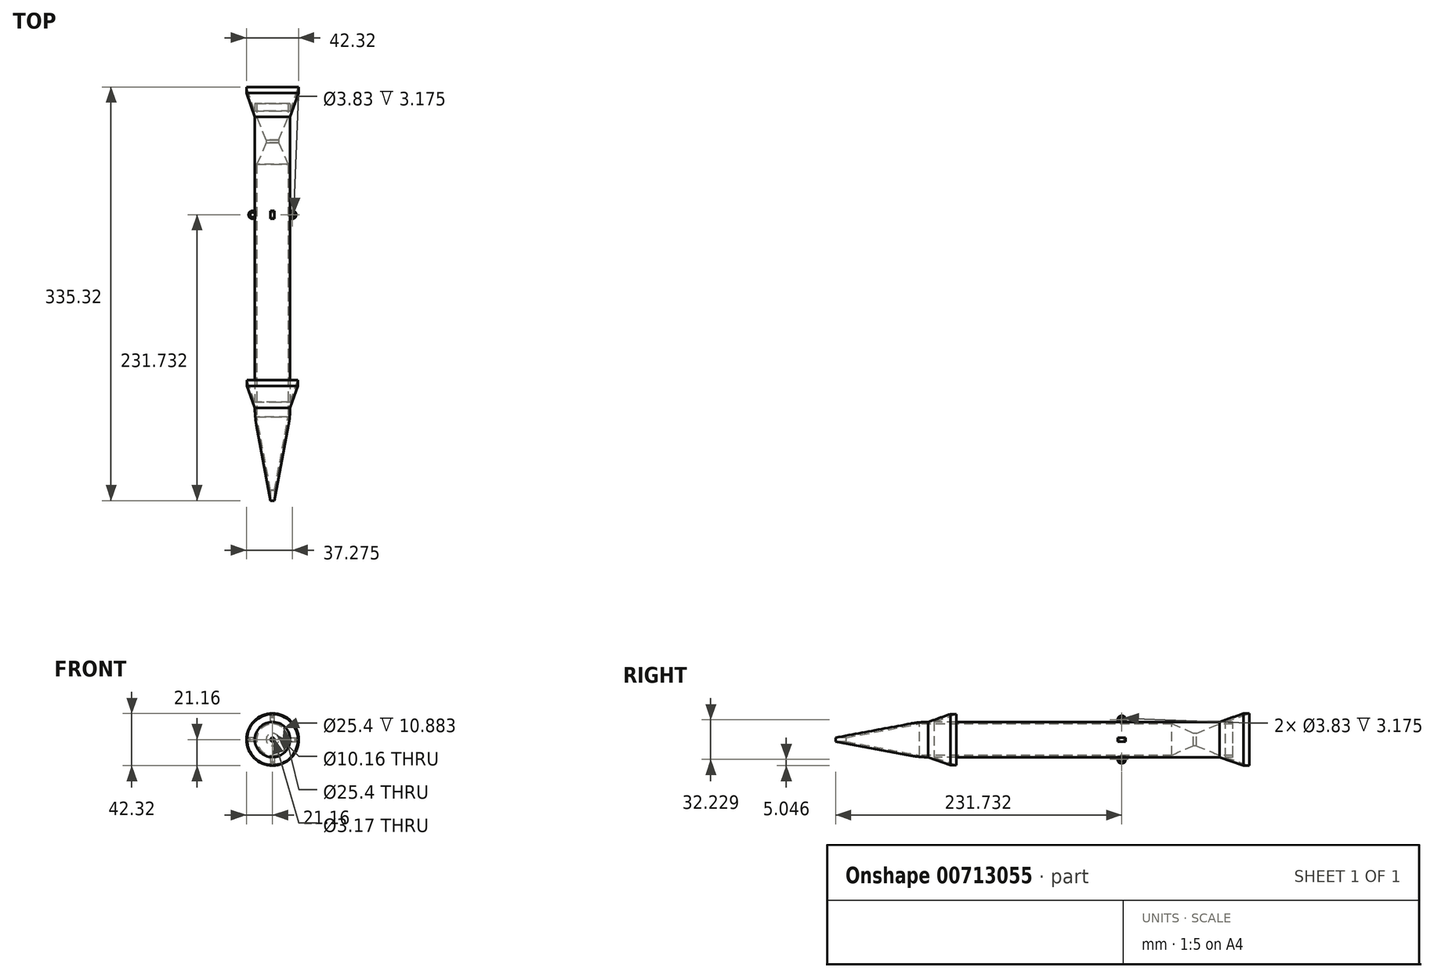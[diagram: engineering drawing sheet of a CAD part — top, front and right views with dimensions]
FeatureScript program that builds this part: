
annotation { "Feature Type Name" : "Feature", "Feature Type Description" : "" }
export const myFeature = defineFeature(function(context is Context, id is Id, definition is map)
    precondition{}
    {
        {
            var Q0;
            Q0=qCreatedBy(makeId("Front.planeOp"),FACE);
            var sketch = newSketch(context, id + "F0", { "sketchPlane" : qUnion([Q0])});
            skCircle(sketch, "E0", {"center": v(0, 0) * mm, "radius": 12.7 * mm});
            skCircle(sketch, "E1", {"center": v(0, 0) * mm, "radius": 14.29 * mm});
            skSolve(sketch);
        }
        {
            var Q0;
            Q0 = qSketchRegion(id + "F0", true);
            extrude(context, id + "F1", {"entities" : qUnion([Q0]), "oppositeDirection" : true, "depth" : 254 * mm, "offsetDistance" : 25.4 * mm});
        }
        {
            var Q0;
            Q0=qCreatedBy(makeId("Top.planeOp"),FACE);
            var sketch = newSketch(context, id + "F2", { "sketchPlane" : qUnion([Q0])});
            skLineSegment(sketch, "E2.0", {"start": v(14.29, 0) * mm, "end": v(-14.29, 0) * mm});
            skLineSegment(sketch, "E3", {"start": v(14.29, 0) * mm, "end": v(1.59, -68) * mm});
            skPoint(sketch, "E4", {"position": v(0, -68) * mm});
            skLineSegment(sketch, "E5", {"start": v(0, -68) * mm, "end": v(0, 0) * mm});
            skLineSegment(sketch, "E6", {"start": v(1.59, -68) * mm, "end": v(1.59, -59.5) * mm});
            skLineSegment(sketch, "E7", {"start": v(1.59, -59.5) * mm, "end": v(12.7, 0) * mm});
            skLineSegment(sketch, "E8.0", {"start": v(12.7, 0) * mm, "end": v(-12.7, 0) * mm});
            skPoint(sketch, "E9.orphan", {"position": v(-1.59, -68) * mm});
            skSolve(sketch);
        }
        {
            var Q0;
            Q0 = qSketchRegion(id + "F2", true);
            var Q1;
            Q1=sQuery(id+"F2.wireOp",EDGE,"E5");
            revolve(context, id + "F3", {"operationType" : NewBodyOperationType.ADD, "surfaceOperationType" : NewSurfaceOperationType.NEW, "entities" : qUnion([Q0]), "axis" : qUnion([Q1]), "revolveType" : RevolveType.FULL});
        }
        {
            var Q0;
            Q0=makeQuery(id+"F3.boolean.opBoolean","MERGE",EDGE,{"derivedFrom":[makeQuery(id+"F1.opExtrude","CAP_EDGE",EDGE,{"disambiguationData":[OSD([sQuery(id+"F0.wireOp",EDGE,"E1")])],"isStart":true}),makeQuery(id+"F3.opRevolve","SWEPT_EDGE",EDGE,{"disambiguationData":[OSD([sQuery(id+"F2.wireOp",EDGE,"E2.0"),sQuery(id+"F2.wireOp",EDGE,"E3")])]})]});
            fillet(context, id + "F4", {"entities" : qUnion([Q0]), "radius" : 76.2 * mm, "tangentPropagation" : true, "allowEdgeOverflow" : false});
        }
        {
            var Q0;
            Q0=qCreatedBy(makeId("Top.planeOp"),FACE);
            var sketch = newSketch(context, id + "F5", { "sketchPlane" : qUnion([Q0])});
            skLineSegment(sketch, "E10", {"start": v(14.29, 254) * mm, "end": v(14.29, 7.06) * mm});
            skLineSegment(sketch, "E11", {"start": v(14.29, 7.06) * mm, "end": v(20.64, 25.02) * mm});
            skLineSegment(sketch, "E12", {"start": v(20.64, 25.02) * mm, "end": v(20.64, 29.78) * mm});
            skLineSegment(sketch, "E13", {"start": v(20.64, 29.78) * mm, "end": v(14.29, 11.82) * mm});
            skLineSegment(sketch, "E14", {"start": v(14.29, 243.12) * mm, "end": v(21.16, 262.57) * mm});
            skLineSegment(sketch, "E15", {"start": v(21.16, 262.57) * mm, "end": v(21.16, 267.33) * mm});
            skLineSegment(sketch, "E16", {"start": v(21.16, 267.33) * mm, "end": v(14.29, 247.88) * mm});
            skLineSegment(sketch, "E17", {"start": v(0, 0) * mm, "end": v(0, 261.94) * mm});
            skSolve(sketch);
        }
        {
            var Q0;
            Q0 = qSketchRegion(id + "F5", true);
            var Q1;
            Q1=sQuery(id+"F5.wireOp",EDGE,"E17");
            revolve(context, id + "F6", {"operationType" : NewBodyOperationType.ADD, "surfaceOperationType" : NewSurfaceOperationType.NEW, "entities" : qUnion([Q0]), "axis" : qUnion([Q1]), "revolveType" : RevolveType.FULL});
        }
        {
            var Q0;
            Q0=qCreatedBy(makeId("Top.planeOp"),FACE);
            var sketch = newSketch(context, id + "F7", { "sketchPlane" : qUnion([Q0])});
            skLineSegment(sketch, "E18", {"start": v(14.29, 243.12) * mm, "end": v(14.29, 11.82) * mm});
            skLineSegment(sketch, "E19", {"start": v(14.29, 166.92) * mm, "end": v(16.2, 166.92) * mm});
            skLineSegment(sketch, "E20", {"start": v(14.29, 160.57) * mm, "end": v(16.2, 160.57) * mm});
            skArc(sketch, "E21", {"start": v(16.2, 160.57) * mm, "mid": v(19.37, 163.74) * mm, "end": v(16.2, 166.92) * mm});
            skPoint(sketch, "E22", {"position": v(19.37, 163.74) * mm});
            skLineSegment(sketch, "E23.0", {"start": v(14.29, 243.12) * mm, "end": v(-14.29, 243.12) * mm});
            skLineSegment(sketch, "E24", {"start": v(0, 0) * mm, "end": v(0, 243.12) * mm});
            skSolve(sketch);
        }
        {
            var Q0;
            Q0 = qSketchRegion(id + "F7", true);
            var Q1;
            Q1=sQuery(id+"F7.wireOp",EDGE,"E24");
            revolve(context, id + "F8", {"operationType" : NewBodyOperationType.ADD, "surfaceOperationType" : NewSurfaceOperationType.NEW, "entities" : qUnion([Q0]), "axis" : qUnion([Q1]), "revolveType" : RevolveType.FULL});
        }
        {
            var Q0;
            Q0=makeQuery(id+"F8.opRevolve","SWEPT_FACE",FACE,{"disambiguationData":[OSD([sQuery(id+"F7.wireOp",EDGE,"E20")])]});
            var sketch = newSketch(context, id + "F9", { "sketchPlane" : qUnion([Q0])});
            skArc(sketch, "E25.0", {"start": v(-14.2, -1.59) * mm, "mid": v(-10.1, -10.1) * mm, "end": v(-1.59, -14.2) * mm});
            skPoint(sketch, "E26", {"position": v(0, 14.29) * mm});
            skPoint(sketch, "E27", {"position": v(14.29, 0) * mm});
            skPoint(sketch, "E28", {"position": v(-14.29, 0) * mm});
            skPoint(sketch, "E29", {"position": v(0, -14.29) * mm});
            skLineSegment(sketch, "E30", {"start": v(1.59, 14.2) * mm, "end": v(1.59, 26.9) * mm});
            skLineSegment(sketch, "E31", {"start": v(-1.59, 26.9) * mm, "end": v(-1.59, 14.2) * mm});
            skPoint(sketch, "E32", {"position": v(0, 26.9) * mm});
            skLineSegment(sketch, "E33", {"start": v(1.59, -14.2) * mm, "end": v(1.59, -26.9) * mm});
            skLineSegment(sketch, "E34", {"start": v(-1.59, -26.9) * mm, "end": v(-1.59, -14.2) * mm});
            skPoint(sketch, "E35", {"position": v(0, -26.9) * mm});
            skLineSegment(sketch, "E36", {"start": v(14.2, 1.59) * mm, "end": v(26.9, 1.59) * mm});
            skLineSegment(sketch, "E37", {"start": v(26.9, -1.59) * mm, "end": v(14.2, -1.59) * mm});
            skPoint(sketch, "E38", {"position": v(26.9, 0) * mm});
            skLineSegment(sketch, "E39", {"start": v(-14.2, -1.59) * mm, "end": v(-26.9, -1.59) * mm});
            skLineSegment(sketch, "E40", {"start": v(-26.9, 1.59) * mm, "end": v(-14.2, 1.59) * mm});
            skPoint(sketch, "E41", {"position": v(-26.9, 0) * mm});
            skArc(sketch, "E42", {"start": v(-26.85, -1.59) * mm, "mid": v(-19.02, -19.02) * mm, "end": v(-1.59, -26.85) * mm});
            skArc(sketch, "E43.trimOffspring", {"start": v(1.59, -14.2) * mm, "mid": v(10.1, -10.1) * mm, "end": v(14.2, -1.59) * mm});
            skArc(sketch, "E44.trimOffspring", {"start": v(-1.59, 14.2) * mm, "mid": v(-10.1, 10.1) * mm, "end": v(-14.2, 1.59) * mm});
            skArc(sketch, "E45.trimOffspring", {"start": v(14.2, 1.59) * mm, "mid": v(10.1, 10.1) * mm, "end": v(1.59, 14.2) * mm});
            skArc(sketch, "E46.trimOffspring", {"start": v(1.59, -26.85) * mm, "mid": v(19.02, -19.02) * mm, "end": v(26.85, -1.59) * mm});
            skArc(sketch, "E47.trimOffspring", {"start": v(-1.59, 26.85) * mm, "mid": v(-19.02, 19.02) * mm, "end": v(-26.85, 1.59) * mm});
            skArc(sketch, "E48.trimOffspring", {"start": v(26.85, 1.59) * mm, "mid": v(19.02, 19.02) * mm, "end": v(1.59, 26.85) * mm});
            skSolve(sketch);
        }
        {
            var Q0;
            Q0 = qSketchRegion(id + "F9", true);
            extrude(context, id + "F10", {"entities" : qUnion([Q0]), "operationType" : NewBodyOperationType.REMOVE, "oppositeDirection" : true, "depth" : 25.4 * mm, "offsetDistance" : 25.4 * mm});
        }
        {
            var Q0;
            Q0=makeQuery(id+"F10.boolean.opBoolean","COPY",FACE,{"derivedFrom":makeQuery(id+"F10.opExtrude","SWEPT_FACE",FACE,{"disambiguationData":[OSD([sQuery(id+"F9.wireOp",EDGE,"E40")])]})});
            var sketch = newSketch(context, id + "F11", { "sketchPlane" : qUnion([Q0])});
            skFitSpline(sketch, "E49.0", {"points": [v(-18.8, 162) * mm, v(-18.48, 161.58) * mm, v(-18.09, 161.23) * mm, v(-17.74, 161) * mm, v(-17.37, 160.81) * mm, v(-16.88, 160.64) * mm, v(-16.25, 160.55) * mm, v(-15.74, 160.58) * mm, v(-15.32, 160.66) * mm, v(-15.03, 160.75) * mm, v(-14.74, 160.87) * mm, v(-14.37, 161.07) * mm, v(-13.95, 161.38) * mm, v(-13.53, 161.85) * mm, v(-13.26, 162.3) * mm, v(-13.1, 162.68) * mm, v(-13, 162.98) * mm, v(-12.95, 163.28) * mm, v(-12.92, 163.6) * mm, v(-12.92, 163.91) * mm, v(-12.95, 164.22) * mm, v(-13.01, 164.53) * mm, v(-13.14, 164.93) * mm, v(-13.36, 165.4) * mm, v(-13.75, 165.9) * mm, v(-14.13, 166.25) * mm, v(-14.48, 166.48) * mm, v(-14.76, 166.62) * mm, v(-15.05, 166.74) * mm, v(-15.35, 166.83) * mm, v(-15.66, 166.89) * mm, v(-16.07, 166.93) * mm, v(-16.6, 166.9) * mm, v(-17.2, 166.75) * mm, v(-17.68, 166.52) * mm, v(-18.02, 166.3) * mm, v(-18.26, 166.1) * mm, v(-18.49, 165.87) * mm, v(-18.68, 165.63) * mm, v(-18.86, 165.37) * mm, v(-19.05, 165) * mm, v(-19.23, 164.51) * mm, v(-19.32, 163.89) * mm, v(-19.3, 163.37) * mm, v(-19.2, 162.96) * mm, v(-19.12, 162.66) * mm, v(-19, 162.37) * mm, v(-18.8, 162) * mm, v(-18.48, 161.58) * mm, v(-18.09, 161.23) * mm]});
            skPoint(sketch, "E50", {"position": v(-16.11, 163.74) * mm});
            skCircle(sketch, "E51", {"center": v(-16.11, 163.74) * mm, "radius": 1.92 * mm});
            skSolve(sketch);
        }
        {
            var Q0;
            Q0 = qSketchRegion(id + "F11", true);
            extrude(context, id + "F12", {"entities" : qUnion([Q0]), "operationType" : NewBodyOperationType.REMOVE, "oppositeDirection" : true, "depth" : 25.4 * mm, "offsetDistance" : 25.4 * mm});
        }
        {
            var Q0;
            Q0=makeQuery(id+"F10.boolean.opBoolean","COPY",FACE,{"derivedFrom":makeQuery(id+"F10.opExtrude","SWEPT_FACE",FACE,{"disambiguationData":[OSD([sQuery(id+"F9.wireOp",EDGE,"E30")])]})});
            var sketch = newSketch(context, id + "F13", { "sketchPlane" : qUnion([Q0])});
            skFitSpline(sketch, "E52.0", {"points": [v(161.2, 14.17) * mm, v(160.92, 14.61) * mm, v(160.72, 15.1) * mm, v(160.62, 15.5) * mm, v(160.56, 15.92) * mm, v(160.56, 16.43) * mm, v(160.69, 17.06) * mm, v(160.89, 17.53) * mm, v(161.1, 17.9) * mm, v(161.29, 18.14) * mm, v(161.5, 18.38) * mm, v(161.73, 18.59) * mm, v(161.98, 18.77) * mm, v(162.34, 18.99) * mm, v(162.82, 19.19) * mm, v(163.33, 19.29) * mm, v(163.75, 19.3) * mm, v(164.06, 19.3) * mm, v(164.37, 19.24) * mm, v(164.68, 19.17) * mm, v(164.97, 19.06) * mm, v(165.25, 18.92) * mm, v(165.52, 18.76) * mm, v(165.86, 18.51) * mm, v(166.22, 18.14) * mm, v(166.57, 17.61) * mm, v(166.76, 17.13) * mm, v(166.86, 16.72) * mm, v(166.9, 16.42) * mm, v(166.92, 16.1) * mm, v(166.9, 15.8) * mm, v(166.86, 15.48) * mm, v(166.78, 15.18) * mm, v(166.68, 14.89) * mm, v(166.5, 14.5) * mm, v(166.21, 14.07) * mm, v(165.76, 13.63) * mm, v(165.33, 13.34) * mm, v(164.95, 13.16) * mm, v(164.66, 13.05) * mm, v(164.36, 12.98) * mm, v(163.94, 12.91) * mm, v(163.42, 12.92) * mm, v(162.8, 13.04) * mm, v(162.33, 13.24) * mm, v(161.97, 13.46) * mm, v(161.72, 13.65) * mm, v(161.49, 13.86) * mm, v(161.2, 14.17) * mm, v(160.92, 14.61) * mm, v(160.72, 15.1) * mm]});
            skPoint(sketch, "E53", {"position": v(163.74, 16.11) * mm});
            skPoint(sketch, "E53.positionSnap0", {"position": v(163.74, 14.2) * mm});
            skCircle(sketch, "E54", {"center": v(163.74, 16.11) * mm, "radius": 1.92 * mm});
            skSolve(sketch);
        }
        {
            var Q0;
            Q0 = qSketchRegion(id + "F13", true);
            extrude(context, id + "F14", {"entities" : qUnion([Q0]), "operationType" : NewBodyOperationType.REMOVE, "oppositeDirection" : true, "depth" : 25.4 * mm, "offsetDistance" : 25.4 * mm});
        }
        {
            var Q0;
            Q0=makeQuery(id+"F10.boolean.opBoolean","COPY",FACE,{"derivedFrom":makeQuery(id+"F10.opExtrude","SWEPT_FACE",FACE,{"disambiguationData":[OSD([sQuery(id+"F9.wireOp",EDGE,"E37")])]})});
            var sketch = newSketch(context, id + "F15", { "sketchPlane" : qUnion([Q0])});
            skFitSpline(sketch, "E55.0", {"points": [v(15.1, -160.72) * mm, v(14.61, -160.92) * mm, v(14.17, -161.2) * mm, v(13.86, -161.48) * mm, v(13.58, -161.8) * mm, v(13.29, -162.22) * mm, v(13.04, -162.8) * mm, v(12.94, -163.31) * mm, v(12.92, -163.73) * mm, v(12.93, -164.04) * mm, v(12.97, -164.35) * mm, v(13.08, -164.76) * mm, v(13.27, -165.24) * mm, v(13.63, -165.76) * mm, v(14, -166.13) * mm, v(14.33, -166.38) * mm, v(14.6, -166.54) * mm, v(14.88, -166.68) * mm, v(15.18, -166.78) * mm, v(15.48, -166.86) * mm, v(15.79, -166.9) * mm, v(16.1, -166.92) * mm, v(16.52, -166.9) * mm, v(17.03, -166.8) * mm, v(17.61, -166.57) * mm, v(18.05, -166.28) * mm, v(18.36, -166) * mm, v(18.57, -165.77) * mm, v(18.76, -165.52) * mm, v(18.92, -165.26) * mm, v(19.06, -164.97) * mm, v(19.2, -164.58) * mm, v(19.3, -164.07) * mm, v(19.3, -163.55) * mm, v(19.25, -163.13) * mm, v(19.17, -162.83) * mm, v(19.07, -162.54) * mm, v(18.94, -162.25) * mm, v(18.77, -161.98) * mm, v(18.59, -161.73) * mm, v(18.38, -161.5) * mm, v(18.07, -161.22) * mm, v(17.64, -160.93) * mm, v(17.05, -160.69) * mm, v(16.55, -160.58) * mm, v(16.13, -160.56) * mm, v(15.81, -160.58) * mm, v(15.5, -160.62) * mm, v(15.1, -160.72) * mm, v(14.61, -160.92) * mm, v(14.17, -161.2) * mm]});
            skPoint(sketch, "E56", {"position": v(16.11, -163.74) * mm});
            skPoint(sketch, "E56.positionSnap0", {"position": v(14.2, -163.74) * mm});
            skCircle(sketch, "E57", {"center": v(16.11, -163.74) * mm, "radius": 1.92 * mm});
            skSolve(sketch);
        }
        {
            var Q0;
            Q0 = qSketchRegion(id + "F15", true);
            extrude(context, id + "F16", {"entities" : qUnion([Q0]), "operationType" : NewBodyOperationType.REMOVE, "oppositeDirection" : true, "depth" : 25.4 * mm, "offsetDistance" : 25.4 * mm});
        }
        {
            var Q0;
            Q0=makeQuery(id+"F10.boolean.opBoolean","COPY",FACE,{"derivedFrom":makeQuery(id+"F10.opExtrude","SWEPT_FACE",FACE,{"disambiguationData":[OSD([sQuery(id+"F9.wireOp",EDGE,"E34")])]})});
            var sketch = newSketch(context, id + "F17", { "sketchPlane" : qUnion([Q0])});
            skFitSpline(sketch, "E58.0", {"points": [v(-162, -18.8) * mm, v(-161.58, -18.48) * mm, v(-161.23, -18.09) * mm, v(-161, -17.74) * mm, v(-160.81, -17.37) * mm, v(-160.64, -16.88) * mm, v(-160.55, -16.25) * mm, v(-160.58, -15.74) * mm, v(-160.66, -15.32) * mm, v(-160.75, -15.03) * mm, v(-160.87, -14.74) * mm, v(-161.07, -14.37) * mm, v(-161.38, -13.95) * mm, v(-161.85, -13.53) * mm, v(-162.3, -13.26) * mm, v(-162.68, -13.1) * mm, v(-162.98, -13) * mm, v(-163.28, -12.95) * mm, v(-163.6, -12.92) * mm, v(-163.91, -12.92) * mm, v(-164.22, -12.95) * mm, v(-164.53, -13.01) * mm, v(-164.93, -13.14) * mm, v(-165.4, -13.36) * mm, v(-165.9, -13.75) * mm, v(-166.25, -14.13) * mm, v(-166.48, -14.48) * mm, v(-166.62, -14.76) * mm, v(-166.74, -15.05) * mm, v(-166.83, -15.35) * mm, v(-166.89, -15.66) * mm, v(-166.93, -16.07) * mm, v(-166.9, -16.6) * mm, v(-166.75, -17.2) * mm, v(-166.52, -17.68) * mm, v(-166.3, -18.02) * mm, v(-166.1, -18.26) * mm, v(-165.87, -18.49) * mm, v(-165.63, -18.68) * mm, v(-165.37, -18.86) * mm, v(-165, -19.05) * mm, v(-164.51, -19.23) * mm, v(-163.89, -19.32) * mm, v(-163.37, -19.3) * mm, v(-162.96, -19.2) * mm, v(-162.66, -19.12) * mm, v(-162.37, -19) * mm, v(-162, -18.8) * mm, v(-161.58, -18.48) * mm, v(-161.23, -18.09) * mm]});
            skPoint(sketch, "E59", {"position": v(-163.74, -16.11) * mm});
            skPoint(sketch, "E59.positionSnap0", {"position": v(-163.74, -14.2) * mm});
            skCircle(sketch, "E60", {"center": v(-163.74, -16.11) * mm, "radius": 1.92 * mm});
            skSolve(sketch);
        }
        {
            var Q0;
            Q0 = qSketchRegion(id + "F17", true);
            extrude(context, id + "F18", {"entities" : qUnion([Q0]), "operationType" : NewBodyOperationType.REMOVE, "oppositeDirection" : true, "depth" : 25.4 * mm, "offsetDistance" : 25.4 * mm});
        }
        {
            var Q0;
            Q0=qCreatedBy(makeId("Top.planeOp"),FACE);
            var sketch = newSketch(context, id + "F19", { "sketchPlane" : qUnion([Q0])});
            skLineSegment(sketch, "E61.0", {"start": v(14.29, 243.12) * mm, "end": v(-14.29, 243.12) * mm});
            skPoint(sketch, "E62", {"position": v(12.7, 243.12) * mm});
            skLineSegment(sketch, "E63", {"start": v(12.7, 243.12) * mm, "end": v(5.08, 224.28) * mm});
            skLineSegment(sketch, "E64", {"start": v(5.08, 224.28) * mm, "end": v(5.08, 222) * mm});
            skLineSegment(sketch, "E65", {"start": v(5.08, 222) * mm, "end": v(12.7, 204.53) * mm});
            skLineSegment(sketch, "E66", {"start": v(12.7, 243.12) * mm, "end": v(12.7, 204.53) * mm});
            skLineSegment(sketch, "E67", {"start": v(0, 0) * mm, "end": v(0, 305.77) * mm});
            skSolve(sketch);
        }
        {
            var Q0;
            Q0 = qSketchRegion(id + "F19", true);
            var Q1;
            Q1=sQuery(id+"F19.wireOp",EDGE,"E67");
            revolve(context, id + "F20", {"operationType" : NewBodyOperationType.ADD, "surfaceOperationType" : NewSurfaceOperationType.NEW, "entities" : qUnion([Q0]), "axis" : qUnion([Q1]), "revolveType" : RevolveType.FULL});
        }
    });
